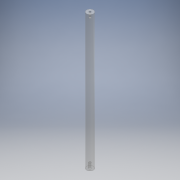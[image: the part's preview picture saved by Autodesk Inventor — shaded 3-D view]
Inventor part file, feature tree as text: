
AUTODESK INVENTOR PART (.ipt)
format: ipt  version: 2016 (Build 200138000, 138)  size: 100,864 bytes
history: native  units: mm
features: other x3, extrude x3, sketch x3
ambient origin geometry x8: Origin, YZ Plane, XZ Plane, XY Plane, X Axis, Y Axis, Z Axis, Center Point
bodies: Body1 (feature_tree)
feature tree (9):
  other  "ソリッド1"
  extrude  "押し出し1"  Depth=8.0mm
  extrude  "押し出し2"  Depth=159.0mm TaperAngle=0.0deg
  extrude  "押し出し3"  Depth=2.5mm
  sketch  "スケッチ1"
  sketch  "スケッチ2"
  sketch  "スケッチ3"
  other  "断面エッジを投影1"
  other  "断面エッジを投影2"
